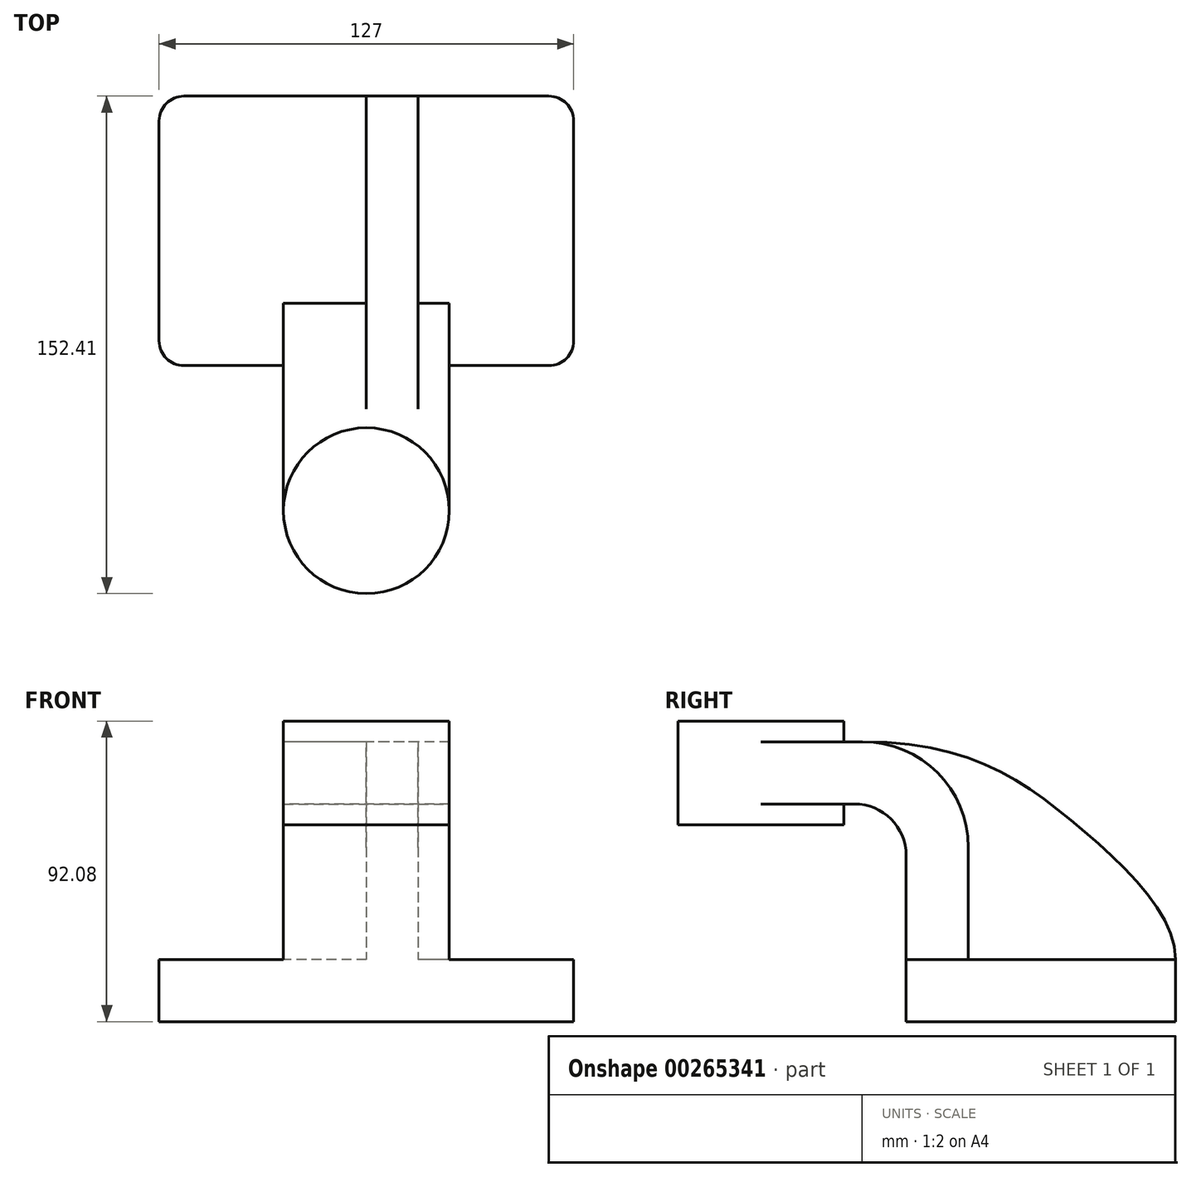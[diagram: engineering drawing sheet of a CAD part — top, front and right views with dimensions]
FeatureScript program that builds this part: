
annotation { "Feature Type Name" : "Feature", "Feature Type Description" : "" }
export const myFeature = defineFeature(function(context is Context, id is Id, definition is map)
    precondition{}
    {
        {
            var Q0;
            Q0=qCreatedBy(makeId("Top.planeOp"),FACE);
            var sketch = newSketch(context, id + "F0", { "sketchPlane" : qUnion([Q0])});
            skLineSegment(sketch, "E0.bottom", {"start": v(55.88, 41.28) * mm, "end": v(-55.88, 41.28) * mm});
            skLineSegment(sketch, "E0.top", {"start": v(55.88, -41.28) * mm, "end": v(-55.88, -41.28) * mm});
            skLineSegment(sketch, "E0.left", {"start": v(63.5, 33.66) * mm, "end": v(63.5, -33.66) * mm});
            skLineSegment(sketch, "E0.right", {"start": v(-63.5, 33.66) * mm, "end": v(-63.5, -33.66) * mm});
            skPoint(sketch, "E0.middle", {"position": v(0, 0) * mm});
            skPoint(sketch, "E1.visualSharp", {"position": v(-63.5, -41.28) * mm});
            skArc(sketch, "E1.filletArc", {"start": v(-63.5, -33.66) * mm, "mid": v(-61.27, -39.04) * mm, "end": v(-55.88, -41.28) * mm});
            skPoint(sketch, "E2.visualSharp", {"position": v(63.5, -41.28) * mm});
            skArc(sketch, "E2.filletArc", {"start": v(55.88, -41.28) * mm, "mid": v(61.27, -39.04) * mm, "end": v(63.5, -33.66) * mm});
            skPoint(sketch, "E3.visualSharp", {"position": v(63.5, 41.28) * mm});
            skArc(sketch, "E3.filletArc", {"start": v(63.5, 33.66) * mm, "mid": v(61.27, 39.04) * mm, "end": v(55.88, 41.28) * mm});
            skPoint(sketch, "E4.visualSharp", {"position": v(-63.5, 41.28) * mm});
            skArc(sketch, "E4.filletArc", {"start": v(-55.88, 41.28) * mm, "mid": v(-61.27, 39.04) * mm, "end": v(-63.5, 33.66) * mm});
            skSolve(sketch);
        }
        {
            var Q0;
            Q0 = qSketchRegion(id + "F0", true);
            extrude(context, id + "F1", {"entities" : qUnion([Q0]), "endBound" : BoundingType.SYMMETRIC, "depth" : 19.05 * mm});
        }
        {
            var Q0;
            Q0=qCreatedBy(makeId("Right.planeOp"),FACE);
            var sketch = newSketch(context, id + "F2", { "sketchPlane" : qUnion([Q0])});
            skLineSegment(sketch, "E5", {"start": v(-22.23, 9.53) * mm, "end": v(-41.28, 9.52) * mm});
            skLineSegment(sketch, "E6", {"start": v(-41.28, 9.52) * mm, "end": v(-41.28, 41.28) * mm});
            skLineSegment(sketch, "E7", {"start": v(-57.15, 57.15) * mm, "end": v(-85.73, 57.15) * mm});
            skLineSegment(sketch, "E8", {"start": v(-85.73, 57.15) * mm, "end": v(-85.73, 76.2) * mm});
            skLineSegment(sketch, "E9", {"start": v(-85.73, 76.2) * mm, "end": v(-54.61, 76.2) * mm});
            skLineSegment(sketch, "E10", {"start": v(-22.23, 43.82) * mm, "end": v(-22.23, 9.53) * mm});
            skPoint(sketch, "E11.visualSharp", {"position": v(-41.28, 57.15) * mm});
            skArc(sketch, "E11.filletArc", {"start": v(-41.28, 41.28) * mm, "mid": v(-45.92, 52.5) * mm, "end": v(-57.15, 57.15) * mm});
            skPoint(sketch, "E12.visualSharp", {"position": v(-22.23, 76.2) * mm});
            skArc(sketch, "E12.filletArc", {"start": v(-22.23, 43.82) * mm, "mid": v(-31.71, 66.71) * mm, "end": v(-54.61, 76.2) * mm});
            skSolve(sketch);
        }
        {
            var Q0;
            Q0 = qSketchRegion(id + "F2", true);
            extrude(context, id + "F3", {"entities" : qUnion([Q0]), "operationType" : NewBodyOperationType.ADD, "endBound" : BoundingType.SYMMETRIC, "depth" : 50.8 * mm});
        }
        {
            var Q0;
            Q0=makeQuery(id+"F3.opExtrude","SWEPT_FACE",FACE,{"disambiguationData":[OSD([sQuery(id+"F2.wireOp",EDGE,"E9")])]});
            var Q1;
            Q1=makeQuery(id+"F3.opExtrude","SWEPT_FACE",FACE,{"disambiguationData":[OSD([sQuery(id+"F2.wireOp",EDGE,"E7")])]});
            cPlane(context, id + "F4", {"entities" : qUnion([Q0, Q1]), "cplaneType" : CPlaneType.MID_PLANE, "offset" : 25.4 * mm, "width" : 152.4 * mm, "height" : 152.4 * mm});
        }
        {
            var Q0;
            Q0=qCreatedBy(id+"F4.planeOp",FACE);
            var sketch = newSketch(context, id + "F5", { "sketchPlane" : qUnion([Q0])});
            skCircle(sketch, "E13", {"center": v(0, -85.73) * mm, "radius": 25.4 * mm});
            skSolve(sketch);
        }
        {
            var Q0;
            Q0 = qSketchRegion(id + "F5", true);
            extrude(context, id + "F6", {"entities" : qUnion([Q0]), "operationType" : NewBodyOperationType.ADD, "endBound" : BoundingType.SYMMETRIC, "depth" : 31.75 * mm});
        }
        {
            var Q0;
            Q0=qCreatedBy(makeId("Right.planeOp"),FACE);
            var sketch = newSketch(context, id + "F7", { "sketchPlane" : qUnion([Q0])});
            skLineSegment(sketch, "E14.0", {"start": v(-22.23, 43.82) * mm, "end": v(-22.23, 9.53) * mm});
            skArc(sketch, "E14.1", {"start": v(-22.23, 43.82) * mm, "mid": v(-31.71, 66.71) * mm, "end": v(-54.61, 76.2) * mm});
            skLineSegment(sketch, "E15", {"start": v(-22.23, 9.53) * mm, "end": v(41.28, 9.53) * mm});
            skFitSpline(sketch, "E16", {"points": [v(-54.61, 76.2) * mm, v(10.99, 50.67) * mm, v(41.28, 9.53) * mm, v(54.62, 9.53) * mm], "startDerivative": vector(220.4, 0) * mm, "endDerivative": vector(274.31, 219.94) * mm});
            skSolve(sketch);
        }
        {
            var Q0;
            Q0 = qSketchRegion(id + "F7", true);
            extrude(context, id + "F8", {"entities" : qUnion([Q0]), "operationType" : NewBodyOperationType.ADD, "depth" : 15.88 * mm});
        }
    });
